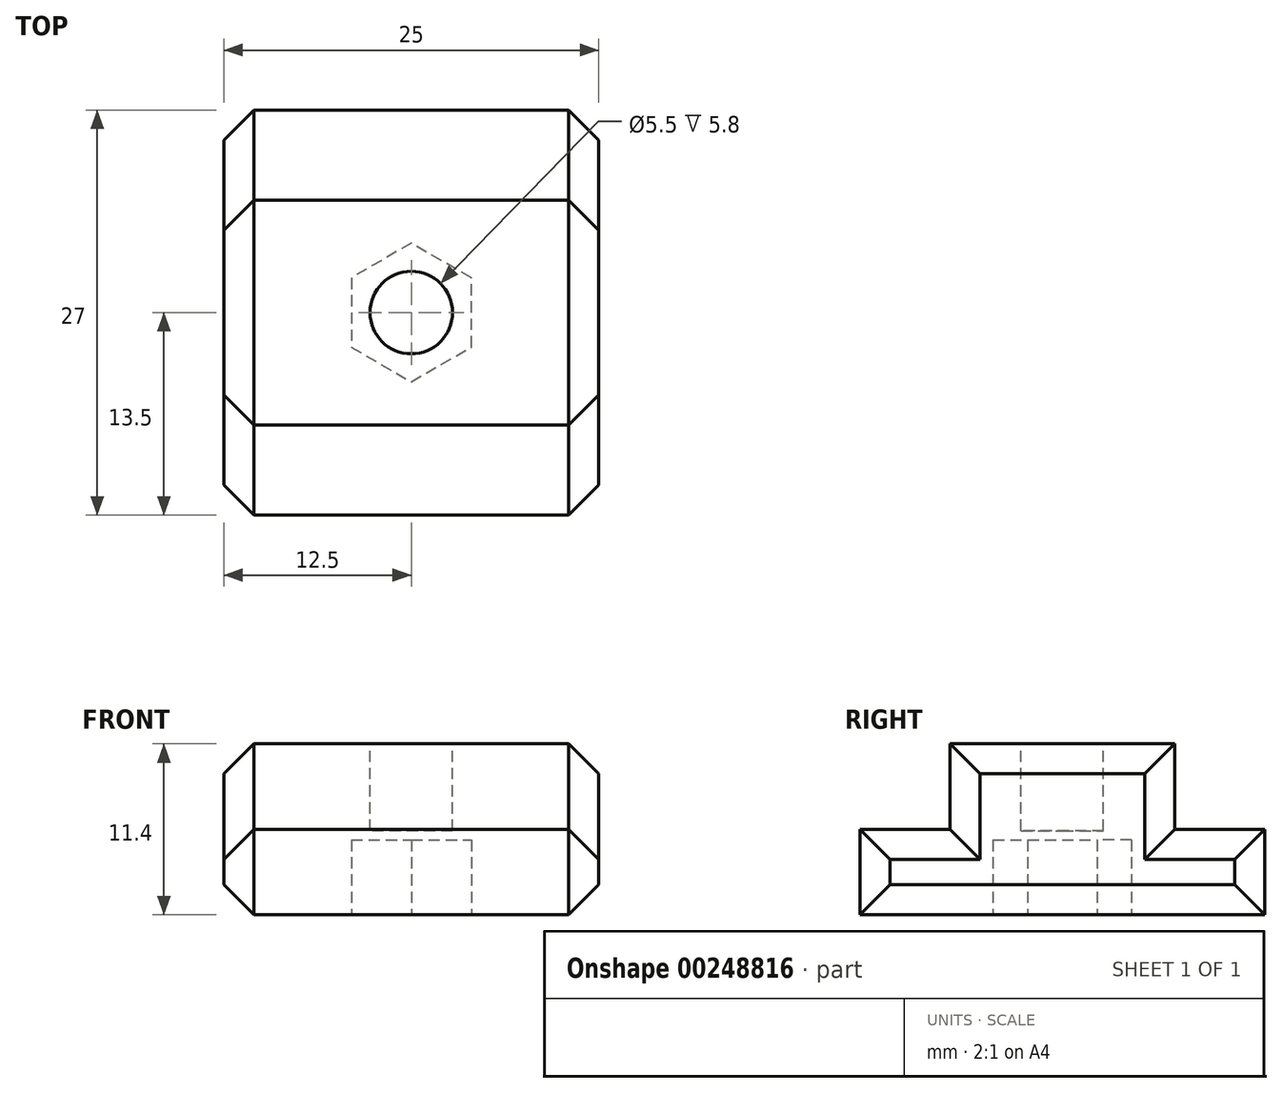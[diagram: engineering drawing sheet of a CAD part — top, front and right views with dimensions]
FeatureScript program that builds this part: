
annotation { "Feature Type Name" : "Feature", "Feature Type Description" : "" }
export const myFeature = defineFeature(function(context is Context, id is Id, definition is map)
    precondition{}
    {
        {
            var Q0;
            Q0=qCreatedBy(makeId("Right.planeOp"),FACE);
            var sketch = newSketch(context, id + "F0", { "sketchPlane" : qUnion([Q0])});
            skLineSegment(sketch, "E0", {"start": v(0, 5.7) * mm, "end": v(7.5, 5.7) * mm});
            skLineSegment(sketch, "E1", {"start": v(7.5, 5.7) * mm, "end": v(7.5, 0) * mm});
            skLineSegment(sketch, "E2", {"start": v(7.5, 0) * mm, "end": v(13.5, 0) * mm});
            skLineSegment(sketch, "E3", {"start": v(13.5, 0) * mm, "end": v(13.5, -5.7) * mm});
            skLineSegment(sketch, "E4", {"start": v(13.5, -5.7) * mm, "end": v(0, -5.7) * mm});
            skLineSegment(sketch, "E5.MirrorCS", {"start": v(0, 5.7) * mm, "end": v(-7.5, 5.7) * mm});
            skLineSegment(sketch, "E6.MirrorCS", {"start": v(-7.5, 0) * mm, "end": v(-13.5, 0) * mm});
            skLineSegment(sketch, "E7.MirrorCS", {"start": v(-13.5, -5.7) * mm, "end": v(0, -5.7) * mm});
            skLineSegment(sketch, "E8.MirrorCS", {"start": v(-7.5, 5.7) * mm, "end": v(-7.5, 0) * mm});
            skLineSegment(sketch, "E9.MirrorCS", {"start": v(-13.5, 0) * mm, "end": v(-13.5, -5.7) * mm});
            skSolve(sketch);
        }
        {
            var Q0;
            Q0=makeQuery(id+"F0.imprint","IMPRINT",FACE,{"disambiguationData":[TD([[makeQuery(id+"F0.imprint","IMPRINT",EDGE,{"derivedFrom":sQuery(id+"F0.wireOp",EDGE,"E0")}),-1.0]])]});
            extrude(context, id + "F1", {"entities" : qUnion([Q0]), "depth" : 25 * mm, "symmetric" : true});
        }
        {
            var Q0;
            Q0=makeQuery(id+"F1.opExtrude","SWEPT_FACE",FACE,{"disambiguationData":[OSD([sQuery(id+"F0.wireOp",EDGE,"E4"),sQuery(id+"F0.wireOp",EDGE,"E7.MirrorCS")])]});
            var sketch = newSketch(context, id + "F2", { "sketchPlane" : qUnion([Q0])});
            skCircle(sketch, "E10.cCircle", {"center": v(0, 0) * mm, "radius": 4 * mm, "construction": true});
            skLineSegment(sketch, "E10.0", {"start": v(4, 2.3) * mm, "end": v(4, -2.3) * mm});
            skLineSegment(sketch, "E10.1", {"start": v(4, -2.3) * mm, "end": v(0, -4.62) * mm});
            skLineSegment(sketch, "E10.2", {"start": v(0, -4.62) * mm, "end": v(-4, -2.3) * mm});
            skLineSegment(sketch, "E10.3", {"start": v(-4, -2.3) * mm, "end": v(-4, 2.3) * mm});
            skLineSegment(sketch, "E10.4", {"start": v(-4, 2.3) * mm, "end": v(0, 4.62) * mm});
            skLineSegment(sketch, "E10.5", {"start": v(0, 4.62) * mm, "end": v(4, 2.3) * mm});
            skPoint(sketch, "E10.0.midPoint", {"position": v(4, 0) * mm});
            skSolve(sketch);
        }
        {
            var Q0;
            Q0=makeQuery(id+"F2.imprint","IMPRINT",FACE,{"disambiguationData":[TD([[makeQuery(id+"F2.imprint","IMPRINT",EDGE,{"derivedFrom":sQuery(id+"F2.wireOp",EDGE,"E10.0")}),-1.0]])]});
            extrude(context, id + "F3", {"entities" : qUnion([Q0]), "operationType" : NewBodyOperationType.REMOVE, "oppositeDirection" : true, "depth" : 5 * mm});
        }
        {
            var Q0;
            Q0=makeQuery(id+"F1.opExtrude","SWEPT_FACE",FACE,{"disambiguationData":[OSD([sQuery(id+"F0.wireOp",EDGE,"E0"),sQuery(id+"F0.wireOp",EDGE,"E5.MirrorCS")])]});
            var sketch = newSketch(context, id + "F4", { "sketchPlane" : qUnion([Q0])});
            skCircle(sketch, "E11", {"center": v(0, 0) * mm, "radius": 2.75 * mm});
            skSolve(sketch);
        }
        {
            var Q0;
            Q0=makeQuery(id+"F4.imprint","IMPRINT",FACE,{"disambiguationData":[TD([[makeQuery(id+"F4.imprint","IMPRINT",EDGE,{"derivedFrom":sQuery(id+"F4.wireOp",EDGE,"E11")}),1.0]])]});
            extrude(context, id + "F5", {"entities" : qUnion([Q0]), "operationType" : NewBodyOperationType.REMOVE, "oppositeDirection" : true, "depth" : 5.8 * mm});
        }
        {
            var Q0;
            Q0=makeQuery(id+"F1.opExtrude","CAP_EDGE",EDGE,{"disambiguationData":[OSD([sQuery(id+"F0.wireOp",EDGE,"E0"),sQuery(id+"F0.wireOp",EDGE,"E5.MirrorCS")])],"isStart":false});
            var Q1;
            Q1=makeQuery(id+"F1.opExtrude","CAP_EDGE",EDGE,{"disambiguationData":[OSD([sQuery(id+"F0.wireOp",EDGE,"E8.MirrorCS")])],"isStart":false});
            var Q2;
            Q2=makeQuery(id+"F1.opExtrude","CAP_EDGE",EDGE,{"disambiguationData":[OSD([sQuery(id+"F0.wireOp",EDGE,"E6.MirrorCS")])],"isStart":false});
            var Q3;
            Q3=makeQuery(id+"F1.opExtrude","CAP_EDGE",EDGE,{"disambiguationData":[OSD([sQuery(id+"F0.wireOp",EDGE,"E2")])],"isStart":false});
            var Q4;
            Q4=makeQuery(id+"F1.opExtrude","CAP_EDGE",EDGE,{"disambiguationData":[OSD([sQuery(id+"F0.wireOp",EDGE,"E1")])],"isStart":false});
            var Q5;
            Q5=makeQuery(id+"F1.opExtrude","CAP_EDGE",EDGE,{"disambiguationData":[OSD([sQuery(id+"F0.wireOp",EDGE,"E9.MirrorCS")])],"isStart":false});
            var Q6;
            Q6=makeQuery(id+"F1.opExtrude","CAP_EDGE",EDGE,{"disambiguationData":[OSD([sQuery(id+"F0.wireOp",EDGE,"E3")])],"isStart":false});
            var Q7;
            Q7=makeQuery(id+"F1.opExtrude","CAP_EDGE",EDGE,{"disambiguationData":[OSD([sQuery(id+"F0.wireOp",EDGE,"E9.MirrorCS")])],"isStart":true});
            var Q8;
            Q8=makeQuery(id+"F1.opExtrude","CAP_EDGE",EDGE,{"disambiguationData":[OSD([sQuery(id+"F0.wireOp",EDGE,"E6.MirrorCS")])],"isStart":true});
            var Q9;
            Q9=makeQuery(id+"F1.opExtrude","CAP_EDGE",EDGE,{"disambiguationData":[OSD([sQuery(id+"F0.wireOp",EDGE,"E8.MirrorCS")])],"isStart":true});
            var Q10;
            Q10=makeQuery(id+"F1.opExtrude","CAP_EDGE",EDGE,{"disambiguationData":[OSD([sQuery(id+"F0.wireOp",EDGE,"E0"),sQuery(id+"F0.wireOp",EDGE,"E5.MirrorCS")])],"isStart":true});
            var Q11;
            Q11=makeQuery(id+"F1.opExtrude","CAP_EDGE",EDGE,{"disambiguationData":[OSD([sQuery(id+"F0.wireOp",EDGE,"E1")])],"isStart":true});
            var Q12;
            Q12=makeQuery(id+"F1.opExtrude","CAP_EDGE",EDGE,{"disambiguationData":[OSD([sQuery(id+"F0.wireOp",EDGE,"E2")])],"isStart":true});
            var Q13;
            Q13=makeQuery(id+"F1.opExtrude","CAP_EDGE",EDGE,{"disambiguationData":[OSD([sQuery(id+"F0.wireOp",EDGE,"E3")])],"isStart":true});
            var Q14;
            Q14=makeQuery(id+"F1.opExtrude","CAP_EDGE",EDGE,{"disambiguationData":[OSD([sQuery(id+"F0.wireOp",EDGE,"E4"),sQuery(id+"F0.wireOp",EDGE,"E7.MirrorCS")])],"isStart":true});
            var Q15;
            Q15=makeQuery(id+"F1.opExtrude","CAP_EDGE",EDGE,{"disambiguationData":[OSD([sQuery(id+"F0.wireOp",EDGE,"E4"),sQuery(id+"F0.wireOp",EDGE,"E7.MirrorCS")])],"isStart":false});
            chamfer(context, id + "F6", {"entities" : qUnion([Q0, Q1, Q2, Q3, Q4, Q5, Q6, Q7, Q8, Q9, Q10, Q11, Q12, Q13, Q14, Q15]), "width" : 2 * mm, "tangentPropagation" : true});
        }
    });
